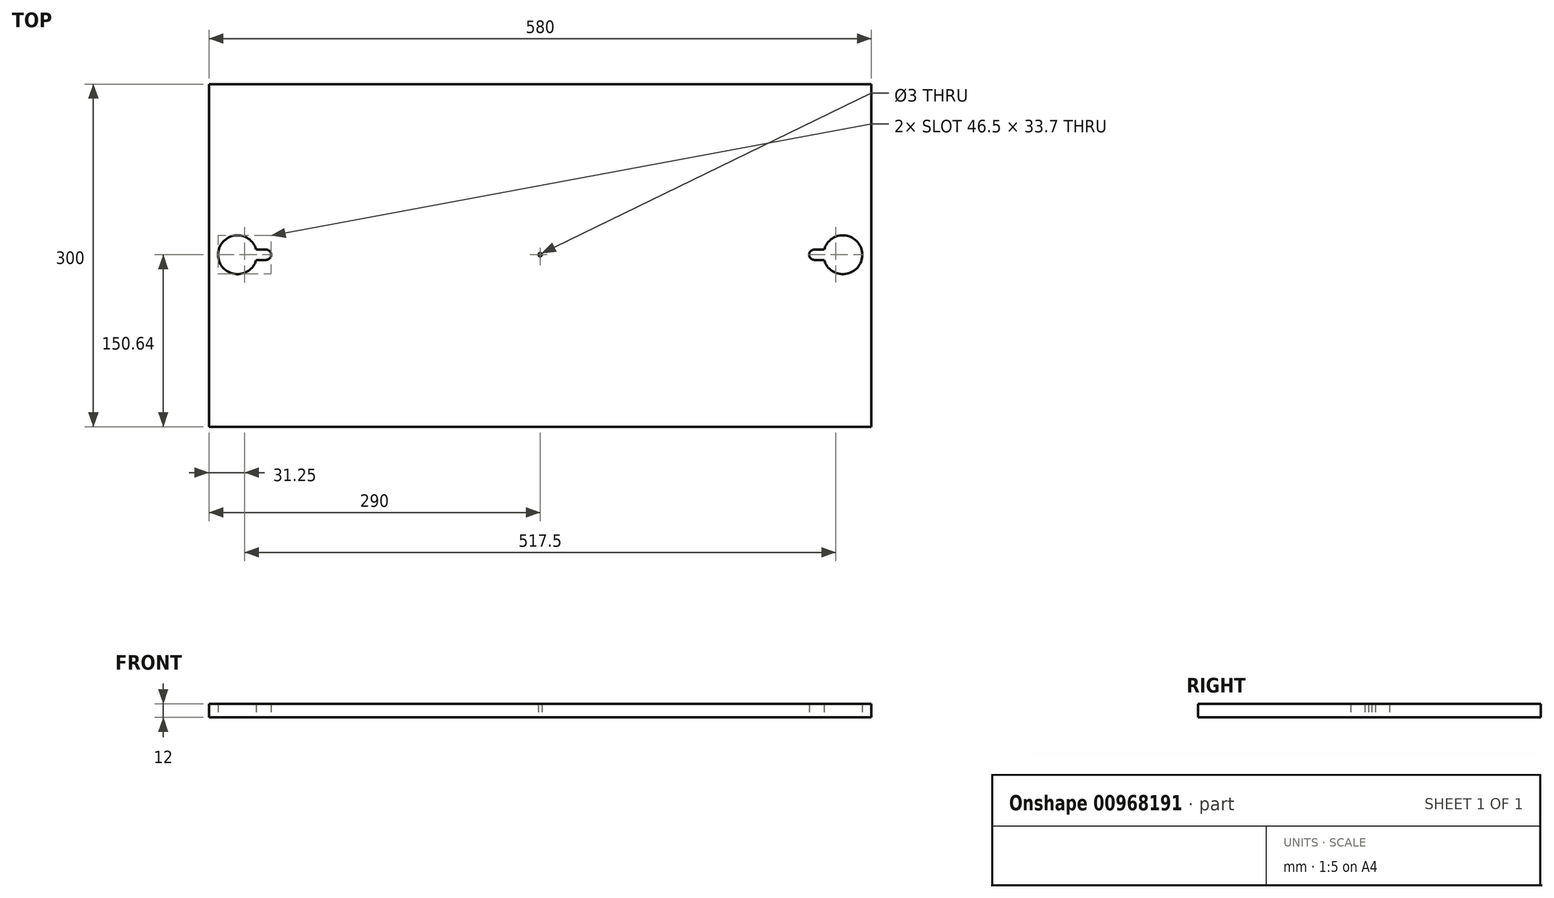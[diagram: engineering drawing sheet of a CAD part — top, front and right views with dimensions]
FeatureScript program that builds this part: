
annotation { "Feature Type Name" : "Feature", "Feature Type Description" : "" }
export const myFeature = defineFeature(function(context is Context, id is Id, definition is map)
    precondition{}
    {
        {
            var Q0;
            Q0=qCreatedBy(makeId("Top.planeOp"),FACE);
            var sketch = newSketch(context, id + "F0", { "sketchPlane" : qUnion([Q0])});
            skLineSegment(sketch, "E0.bottom", {"start": v(0, 149.36) * mm, "end": v(290, 149.36) * mm});
            skLineSegment(sketch, "E0.top", {"start": v(0, -150.64) * mm, "end": v(290, -150.64) * mm});
            skLineSegment(sketch, "E0.left", {"start": v(0, 149.36) * mm, "end": v(0, -150.64) * mm});
            skLineSegment(sketch, "E0.right", {"start": v(290, 149.36) * mm, "end": v(290, -150.64) * mm});
            skLineSegment(sketch, "E1", {"start": v(0, 0) * mm, "end": v(401.29, 0) * mm, "construction": true});
            skPoint(sketch, "E2", {"position": v(0, 0) * mm});
            skPoint(sketch, "E3", {"position": v(240, 0) * mm});
            skPoint(sketch, "E4", {"position": v(265, 0) * mm});
            skCircle(sketch, "E5", {"center": v(240, 0) * mm, "radius": 4.5 * mm});
            skCircle(sketch, "E6", {"center": v(0, 0) * mm, "radius": 1.5 * mm});
            skLineSegment(sketch, "E7.MirrorCS", {"start": v(0, 149.36) * mm, "end": v(-290, 149.36) * mm});
            skLineSegment(sketch, "E8.MirrorCS", {"start": v(0, -150.64) * mm, "end": v(-290, -150.64) * mm});
            skLineSegment(sketch, "E9.MirrorCS", {"start": v(-290, 149.36) * mm, "end": v(-290, -150.64) * mm});
            skCircle(sketch, "E10.MirrorC", {"center": v(-240, 0) * mm, "radius": 4.5 * mm});
            skCircle(sketch, "E11", {"center": v(265, 0) * mm, "radius": 17 * mm});
            skLineSegment(sketch, "E12", {"start": v(240, 14.31) * mm, "end": v(240, -31.36) * mm, "construction": true});
            skLineSegment(sketch, "E13", {"start": v(240, 4.5) * mm, "end": v(248.6, 4.5) * mm});
            skLineSegment(sketch, "E14", {"start": v(240, -4.5) * mm, "end": v(248.6, -4.5) * mm});
            skLineSegment(sketch, "E15.MirrorCS", {"start": v(-240, 4.5) * mm, "end": v(-248.6, 4.5) * mm});
            skLineSegment(sketch, "E16.MirrorCS", {"start": v(-240, -4.5) * mm, "end": v(-248.6, -4.5) * mm});
            skCircle(sketch, "E17.MirrorC", {"center": v(-265, 0) * mm, "radius": 17 * mm});
            skSolve(sketch);
        }
        {
            var Q0;
            Q0 = qSketchRegion(id + "F0", true);
            extrude(context, id + "F1", {"entities" : qUnion([Q0]), "depth" : 12 * mm, "offsetDistance" : 25 * mm});
        }
    });
